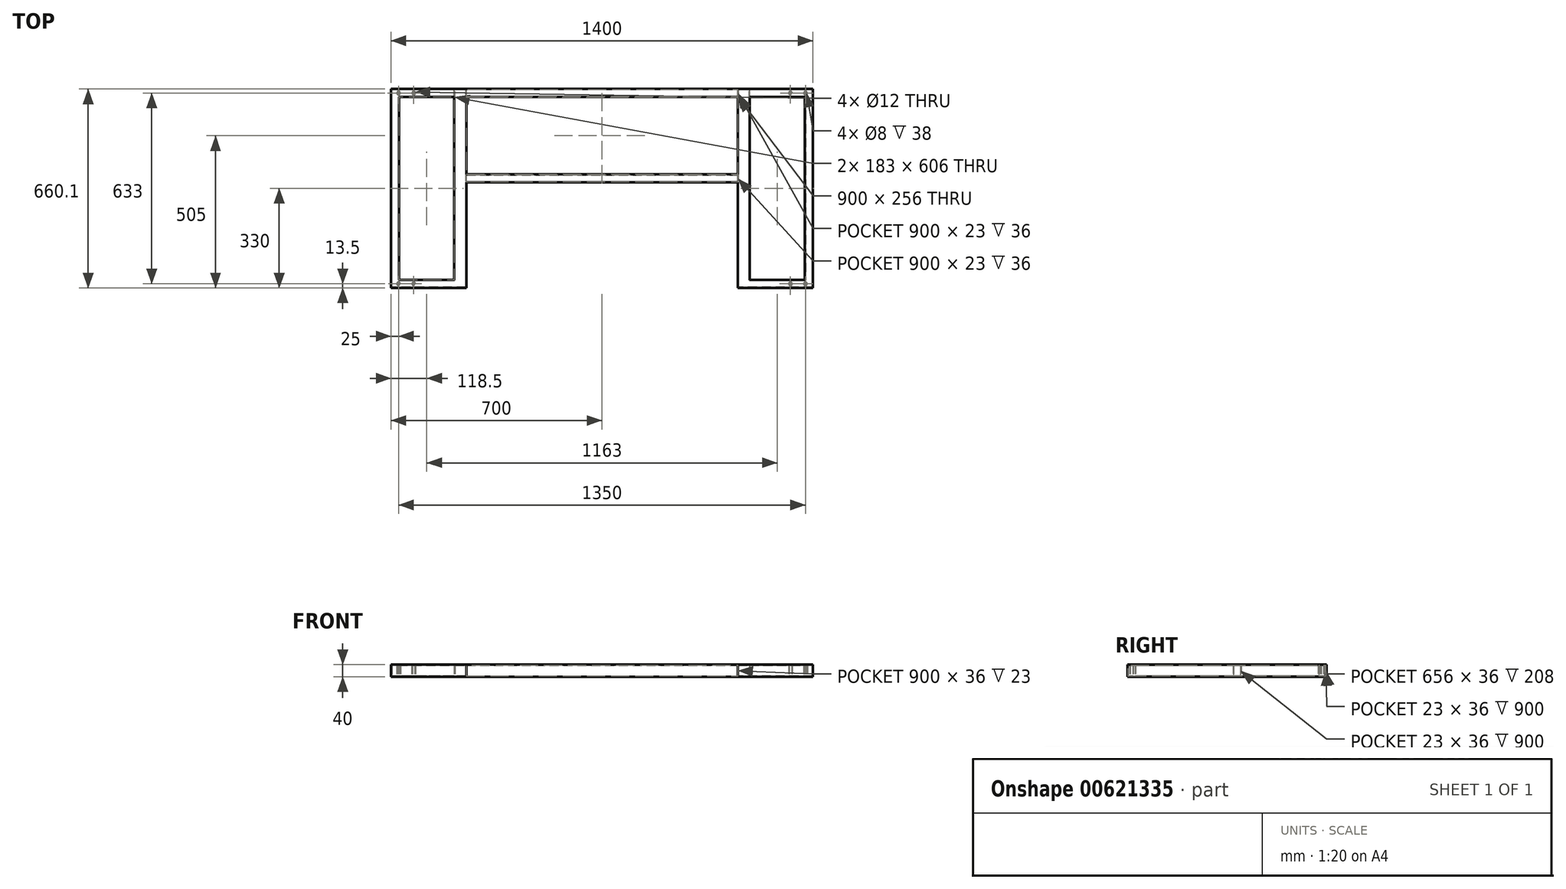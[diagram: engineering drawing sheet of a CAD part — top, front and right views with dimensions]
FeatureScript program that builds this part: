
annotation { "Feature Type Name" : "Feature", "Feature Type Description" : "" }
export const myFeature = defineFeature(function(context is Context, id is Id, definition is map)
    precondition{}
    {
        {
            var Q0;
            Q0=qCreatedBy(makeId("Top.planeOp"),FACE);
            var sketch = newSketch(context, id + "F0", { "sketchPlane" : qUnion([Q0])});
            skLineSegment(sketch, "E0.bottom", {"start": v(700, -330) * mm, "end": v(-700, -330) * mm});
            skLineSegment(sketch, "E0.top", {"start": v(700, 330) * mm, "end": v(-700, 330) * mm});
            skLineSegment(sketch, "E0.left", {"start": v(700, -330) * mm, "end": v(700, 330) * mm});
            skLineSegment(sketch, "E0.right", {"start": v(-700, -330) * mm, "end": v(-700, 330) * mm});
            skPoint(sketch, "E0.middle", {"position": v(0, 0) * mm});
            skLineSegment(sketch, "E1.bottom", {"start": v(-450, -330) * mm, "end": v(450, -330) * mm});
            skLineSegment(sketch, "E1.top", {"start": v(-450, 20) * mm, "end": v(450, 20) * mm});
            skLineSegment(sketch, "E1.left", {"start": v(-450, -330) * mm, "end": v(-450, 20) * mm});
            skLineSegment(sketch, "E1.right", {"start": v(450, -330) * mm, "end": v(450, 20) * mm});
            skLineSegment(sketch, "E2.bottom", {"start": v(-673, 303) * mm, "end": v(-490, 303) * mm});
            skLineSegment(sketch, "E2.top", {"start": v(-673, -303) * mm, "end": v(-490, -303) * mm});
            skLineSegment(sketch, "E2.left", {"start": v(-673, 303) * mm, "end": v(-673, -303) * mm});
            skLineSegment(sketch, "E2.right", {"start": v(-490, 303) * mm, "end": v(-490, -303) * mm});
            skLineSegment(sketch, "E3.bottom", {"start": v(490, 303) * mm, "end": v(673, 303) * mm});
            skLineSegment(sketch, "E3.top", {"start": v(490, -303) * mm, "end": v(673, -303) * mm});
            skLineSegment(sketch, "E3.left", {"start": v(490, 303) * mm, "end": v(490, -303) * mm});
            skLineSegment(sketch, "E3.right", {"start": v(673, 303) * mm, "end": v(673, -303) * mm});
            skLineSegment(sketch, "E4.bottom", {"start": v(-450, 303) * mm, "end": v(450, 303) * mm});
            skLineSegment(sketch, "E4.top", {"start": v(-450, 47) * mm, "end": v(450, 47) * mm});
            skLineSegment(sketch, "E4.left", {"start": v(-450, 303) * mm, "end": v(-450, 47) * mm});
            skLineSegment(sketch, "E4.right", {"start": v(450, 303) * mm, "end": v(450, 47) * mm});
            skLineSegment(sketch, "E5.bottom", {"start": v(-490, 303) * mm, "end": v(-450, 303) * mm});
            skLineSegment(sketch, "E5.top", {"start": v(-490, 330.1) * mm, "end": v(-450, 330.1) * mm});
            skLineSegment(sketch, "E5.left", {"start": v(-490, 303) * mm, "end": v(-490, 330.1) * mm});
            skLineSegment(sketch, "E5.right", {"start": v(-450, 303) * mm, "end": v(-450, 330.1) * mm});
            skLineSegment(sketch, "E6.bottom", {"start": v(450, 303) * mm, "end": v(490, 303) * mm});
            skLineSegment(sketch, "E6.top", {"start": v(450, 330.1) * mm, "end": v(490, 330.1) * mm});
            skLineSegment(sketch, "E6.left", {"start": v(450, 303) * mm, "end": v(450, 330.1) * mm});
            skLineSegment(sketch, "E6.right", {"start": v(490, 303) * mm, "end": v(490, 330.1) * mm});
            skSolve(sketch);
        }
        {
            var Q0;
            {var subQ5=sQuery(id+"F0.wireOp",EDGE,"E6.top");Q0=makeQuery(id+"F0.imprint","IMPRINT",FACE,{"disambiguationData":[TD([[makeQuery(id+"F0.imprint","IMPRINT",EDGE,{"derivedFrom":subQ5}),-1.0]])]});}
            var Q1;
            {var subQ5=sQuery(id+"F0.wireOp",EDGE,"E5.top");Q1=makeQuery(id+"F0.imprint","IMPRINT",FACE,{"disambiguationData":[TD([[makeQuery(id+"F0.imprint","IMPRINT",EDGE,{"derivedFrom":subQ5}),-1.0]])]});}
            var Q2;
            {var subQ5=sQuery(id+"F0.wireOp",EDGE,"E6.bottom");Q2=makeQuery(id+"F0.imprint","IMPRINT",FACE,{"disambiguationData":[TD([[makeQuery(id+"F0.imprint","IMPRINT",EDGE,{"derivedFrom":subQ5}),1.0]])]});}
            var Q3;
            {var subQ5=sQuery(id+"F0.wireOp",EDGE,"E4.bottom");Q3=makeQuery(id+"F0.imprint","IMPRINT",FACE,{"disambiguationData":[TD([[makeQuery(id+"F0.imprint","IMPRINT",EDGE,{"derivedFrom":subQ5}),1.0]])]});}
            var Q4;
            {var subQ5=sQuery(id+"F0.wireOp",EDGE,"E5.bottom");Q4=makeQuery(id+"F0.imprint","IMPRINT",FACE,{"disambiguationData":[TD([[makeQuery(id+"F0.imprint","IMPRINT",EDGE,{"derivedFrom":subQ5}),1.0]])]});}
            var Q5;
            {var subQ9=sQuery(id+"F0.wireOp",EDGE,"E0.left");Q5=makeQuery(id+"F0.imprint","IMPRINT",FACE,{"disambiguationData":[TD([[makeQuery(id+"F0.imprint","IMPRINT",EDGE,{"derivedFrom":subQ9}),1.0]])]});}
            extrude(context, id + "F1", {"entities" : qUnion([Q0, Q1, Q2, Q3, Q4, Q5]), "depth" : 40 * mm, "offsetDistance" : 25 * mm});
        }
        {
            var Q0;
            Q0=makeQuery(id+"F1.opExtrude","SWEPT_FACE",FACE,{"disambiguationData":[OSD([sQuery(id+"F0.wireOp",EDGE,"E5.top")])]});
            var Q1;
            Q1=makeQuery(id+"F1.opExtrude","SWEPT_FACE",FACE,{"disambiguationData":[OSD([sQuery(id+"F0.wireOp",EDGE,"E6.top")])]});
            shell(context, id + "F2", {"entities" : qUnion([Q0, Q1]), "thickness" : 2 * mm});
        }
        {
            var Q0;
            Q0=makeQuery(id+"F1.opExtrude","SWEPT_FACE",FACE,{"disambiguationData":[OSD([sQuery(id+"F0.wireOp",EDGE,"E6.top")])]});
            var Q1;
            Q1=makeQuery(id+"F1.opExtrude","SWEPT_FACE",FACE,{"disambiguationData":[OSD([sQuery(id+"F0.wireOp",EDGE,"E5.top")])]});
            extrude(context, id + "F3", {"entities" : qUnion([Q0, Q1]), "operationType" : NewBodyOperationType.ADD, "oppositeDirection" : true, "depth" : 390 * mm, "offsetDistance" : 25 * mm});
        }
        {
            var Q0;
            Q0=makeQuery(id+"F1.opExtrude","CAP_FACE",FACE,{"disambiguationData":[OSD([sQuery(id+"F0.wireOp",EDGE,"E0.bottom"),sQuery(id+"F0.wireOp",EDGE,"E0.top"),sQuery(id+"F0.wireOp",EDGE,"E0.left"),sQuery(id+"F0.wireOp",EDGE,"E0.right"),sQuery(id+"F0.wireOp",EDGE,"E1.top"),sQuery(id+"F0.wireOp",EDGE,"E1.left"),sQuery(id+"F0.wireOp",EDGE,"E1.right"),sQuery(id+"F0.wireOp",EDGE,"E2.bottom"),sQuery(id+"F0.wireOp",EDGE,"E2.top"),sQuery(id+"F0.wireOp",EDGE,"E2.left"),sQuery(id+"F0.wireOp",EDGE,"E2.right"),sQuery(id+"F0.wireOp",EDGE,"E3.bottom"),sQuery(id+"F0.wireOp",EDGE,"E3.top"),sQuery(id+"F0.wireOp",EDGE,"E3.left"),sQuery(id+"F0.wireOp",EDGE,"E3.right"),sQuery(id+"F0.wireOp",EDGE,"E4.bottom"),sQuery(id+"F0.wireOp",EDGE,"E4.top"),sQuery(id+"F0.wireOp",EDGE,"E4.left"),sQuery(id+"F0.wireOp",EDGE,"E4.right"),sQuery(id+"F0.wireOp",EDGE,"E5.top"),sQuery(id+"F0.wireOp",EDGE,"E5.left"),sQuery(id+"F0.wireOp",EDGE,"E5.right"),sQuery(id+"F0.wireOp",EDGE,"E6.top"),sQuery(id+"F0.wireOp",EDGE,"E6.left"),sQuery(id+"F0.wireOp",EDGE,"E6.right")])],"isStart":true});
            var sketch = newSketch(context, id + "F4", { "sketchPlane" : qUnion([Q0])});
            skCircle(sketch, "E7", {"center": v(-675, 316.5) * mm, "radius": 4 * mm});
            skCircle(sketch, "E8", {"center": v(-625, 316.5) * mm, "radius": 4 * mm});
            skCircle(sketch, "E9.MirrorC", {"center": v(675, 316.5) * mm, "radius": 4 * mm});
            skCircle(sketch, "E10.MirrorC", {"center": v(625, 316.5) * mm, "radius": 4 * mm});
            skCircle(sketch, "E11.MirrorC", {"center": v(-675, -316.5) * mm, "radius": 4 * mm});
            skCircle(sketch, "E12.MirrorC", {"center": v(-625, -316.5) * mm, "radius": 4 * mm});
            skCircle(sketch, "E13.MirrorC", {"center": v(625, -316.5) * mm, "radius": 4 * mm});
            skCircle(sketch, "E14.MirrorC", {"center": v(675, -316.5) * mm, "radius": 4 * mm});
            skCircle(sketch, "E15", {"center": v(-675, 316.5) * mm, "radius": 6 * mm});
            skCircle(sketch, "E16", {"center": v(-625, 316.5) * mm, "radius": 6 * mm});
            skCircle(sketch, "E17.MirrorC", {"center": v(675, 316.5) * mm, "radius": 6 * mm});
            skCircle(sketch, "E18.MirrorC", {"center": v(625, 316.5) * mm, "radius": 6 * mm});
            skCircle(sketch, "E19.MirrorC", {"center": v(625, -316.5) * mm, "radius": 6 * mm});
            skCircle(sketch, "E20.MirrorC", {"center": v(675, -316.5) * mm, "radius": 6 * mm});
            skCircle(sketch, "E21.MirrorC", {"center": v(-675, -316.5) * mm, "radius": 6 * mm});
            skCircle(sketch, "E22.MirrorC", {"center": v(-625, -316.5) * mm, "radius": 6 * mm});
            skSolve(sketch);
        }
        {
            var Q0;
            Q0=makeQuery(id+"F4.imprint","IMPRINT",FACE,{"disambiguationData":[TD([[makeQuery(id+"F4.imprint","IMPRINT",EDGE,{"derivedFrom":sQuery(id+"F4.wireOp",EDGE,"E11.MirrorC")}),-1.0]])]});
            var Q1;
            Q1=makeQuery(id+"F4.imprint","IMPRINT",FACE,{"disambiguationData":[TD([[makeQuery(id+"F4.imprint","IMPRINT",EDGE,{"derivedFrom":sQuery(id+"F4.wireOp",EDGE,"E12.MirrorC")}),-1.0]])]});
            var Q2;
            Q2=makeQuery(id+"F4.imprint","IMPRINT",FACE,{"disambiguationData":[TD([[makeQuery(id+"F4.imprint","IMPRINT",EDGE,{"derivedFrom":sQuery(id+"F4.wireOp",EDGE,"E14.MirrorC")}),1.0]])]});
            var Q3;
            Q3=makeQuery(id+"F4.imprint","IMPRINT",FACE,{"disambiguationData":[TD([[makeQuery(id+"F4.imprint","IMPRINT",EDGE,{"derivedFrom":sQuery(id+"F4.wireOp",EDGE,"E13.MirrorC")}),1.0]])]});
            var Q4;
            Q4=makeQuery(id+"F4.imprint","IMPRINT",FACE,{"disambiguationData":[TD([[makeQuery(id+"F4.imprint","IMPRINT",EDGE,{"derivedFrom":sQuery(id+"F4.wireOp",EDGE,"E7")}),1.0]])]});
            var Q5;
            Q5=makeQuery(id+"F4.imprint","IMPRINT",FACE,{"disambiguationData":[TD([[makeQuery(id+"F4.imprint","IMPRINT",EDGE,{"derivedFrom":sQuery(id+"F4.wireOp",EDGE,"E8")}),1.0]])]});
            var Q6;
            Q6=makeQuery(id+"F4.imprint","IMPRINT",FACE,{"disambiguationData":[TD([[makeQuery(id+"F4.imprint","IMPRINT",EDGE,{"derivedFrom":sQuery(id+"F4.wireOp",EDGE,"E9.MirrorC")}),-1.0]])]});
            var Q7;
            Q7=makeQuery(id+"F4.imprint","IMPRINT",FACE,{"disambiguationData":[TD([[makeQuery(id+"F4.imprint","IMPRINT",EDGE,{"derivedFrom":sQuery(id+"F4.wireOp",EDGE,"E10.MirrorC")}),-1.0]])]});
            extrude(context, id + "F5", {"entities" : qUnion([Q0, Q1, Q2, Q3, Q4, Q5, Q6, Q7]), "operationType" : NewBodyOperationType.REMOVE, "oppositeDirection" : true, "depth" : 25 * mm, "offsetDistance" : 25 * mm});
        }
        {
            var Q0;
            Q0=makeQuery(id+"F4.imprint","IMPRINT",FACE,{"disambiguationData":[TD([[makeQuery(id+"F4.imprint","IMPRINT",EDGE,{"derivedFrom":sQuery(id+"F4.wireOp",EDGE,"E11.MirrorC")}),1.0]])]});
            var Q1;
            Q1=makeQuery(id+"F4.imprint","IMPRINT",FACE,{"disambiguationData":[TD([[makeQuery(id+"F4.imprint","IMPRINT",EDGE,{"derivedFrom":sQuery(id+"F4.wireOp",EDGE,"E12.MirrorC")}),1.0]])]});
            var Q2;
            Q2=makeQuery(id+"F4.imprint","IMPRINT",FACE,{"disambiguationData":[TD([[makeQuery(id+"F4.imprint","IMPRINT",EDGE,{"derivedFrom":sQuery(id+"F4.wireOp",EDGE,"E7")}),-1.0]])]});
            var Q3;
            Q3=makeQuery(id+"F4.imprint","IMPRINT",FACE,{"disambiguationData":[TD([[makeQuery(id+"F4.imprint","IMPRINT",EDGE,{"derivedFrom":sQuery(id+"F4.wireOp",EDGE,"E8")}),-1.0]])]});
            var Q4;
            Q4=makeQuery(id+"F4.imprint","IMPRINT",FACE,{"disambiguationData":[TD([[makeQuery(id+"F4.imprint","IMPRINT",EDGE,{"derivedFrom":sQuery(id+"F4.wireOp",EDGE,"E9.MirrorC")}),1.0]])]});
            var Q5;
            Q5=makeQuery(id+"F4.imprint","IMPRINT",FACE,{"disambiguationData":[TD([[makeQuery(id+"F4.imprint","IMPRINT",EDGE,{"derivedFrom":sQuery(id+"F4.wireOp",EDGE,"E10.MirrorC")}),1.0]])]});
            var Q6;
            Q6=makeQuery(id+"F4.imprint","IMPRINT",FACE,{"disambiguationData":[TD([[makeQuery(id+"F4.imprint","IMPRINT",EDGE,{"derivedFrom":sQuery(id+"F4.wireOp",EDGE,"E14.MirrorC")}),-1.0]])]});
            var Q7;
            Q7=makeQuery(id+"F4.imprint","IMPRINT",FACE,{"disambiguationData":[TD([[makeQuery(id+"F4.imprint","IMPRINT",EDGE,{"derivedFrom":sQuery(id+"F4.wireOp",EDGE,"E13.MirrorC")}),-1.0]])]});
            extrude(context, id + "F6", {"entities" : qUnion([Q0, Q1, Q2, Q3, Q4, Q5, Q6, Q7]), "operationType" : NewBodyOperationType.ADD, "oppositeDirection" : true, "depth" : 40 * mm, "offsetDistance" : 25 * mm});
        }
    });
